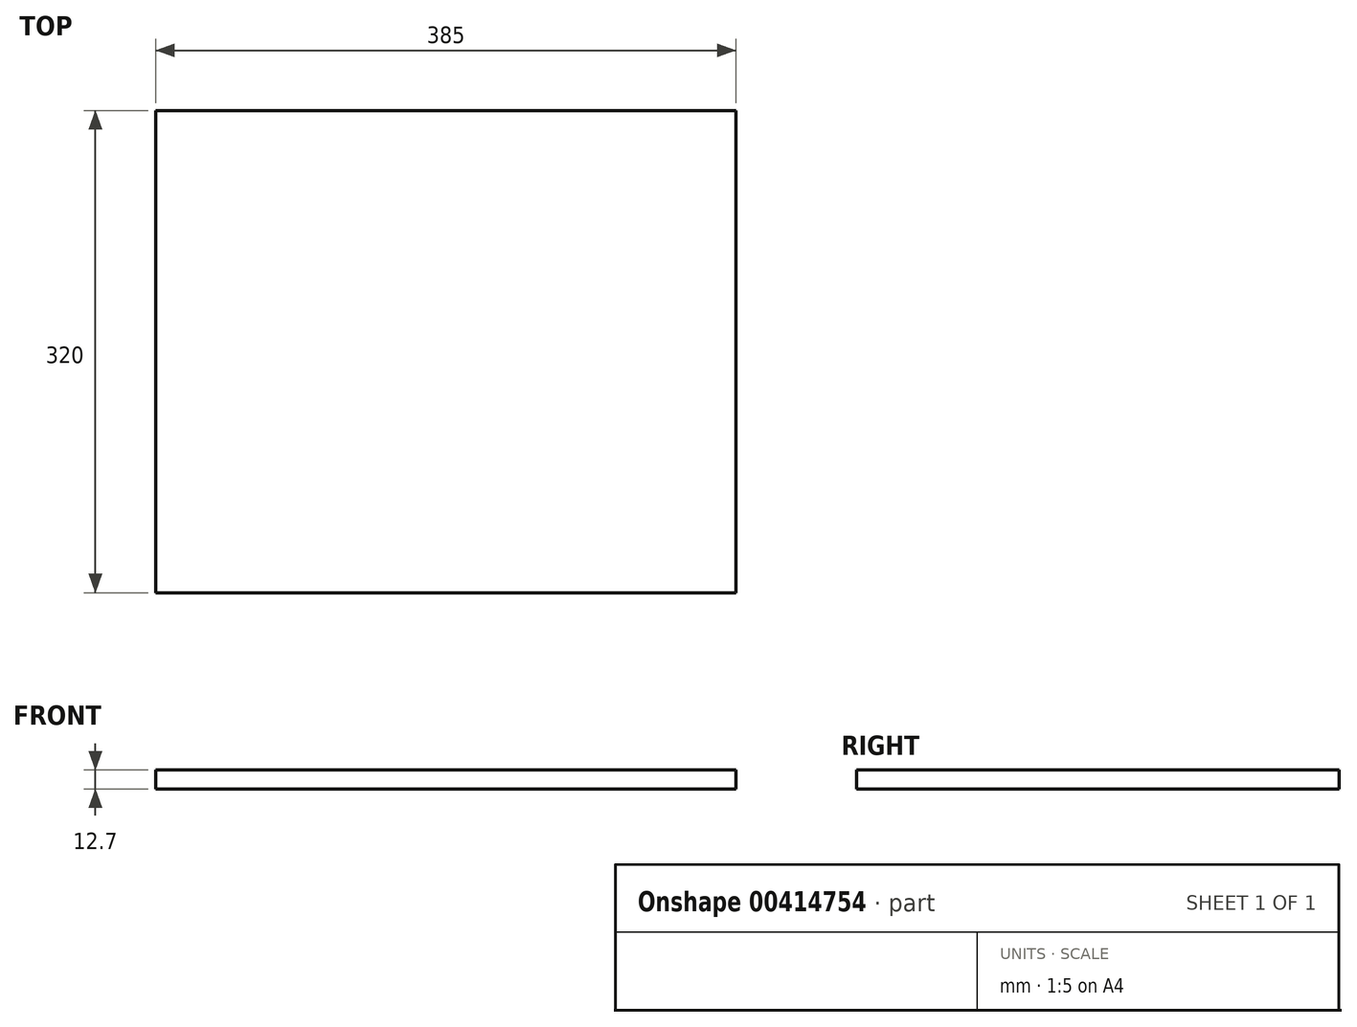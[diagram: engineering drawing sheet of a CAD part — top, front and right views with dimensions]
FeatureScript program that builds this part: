
annotation { "Feature Type Name" : "Feature", "Feature Type Description" : "" }
export const myFeature = defineFeature(function(context is Context, id is Id, definition is map)
    precondition{}
    {
        {
            var Q0;
            Q0=qCreatedBy(makeId("Top.planeOp"),FACE);
            var sketch = newSketch(context, id + "F0", { "sketchPlane" : qUnion([Q0])});
            skLineSegment(sketch, "E0.bottom", {"start": v(-70.96, 65.05) * mm, "end": v(314.04, 65.05) * mm});
            skLineSegment(sketch, "E0.top", {"start": v(-70.96, -254.95) * mm, "end": v(314.04, -254.95) * mm});
            skLineSegment(sketch, "E0.left", {"start": v(-70.96, 65.05) * mm, "end": v(-70.96, -254.95) * mm});
            skLineSegment(sketch, "E0.right", {"start": v(314.04, 65.05) * mm, "end": v(314.04, -254.95) * mm});
            skSolve(sketch);
        }
        {
            var Q0;
            Q0=qSketchRegion(id+"F0",true);
            extrude(context, id + "F1", {"entities" : qUnion([Q0]), "depth" : 12.7 * mm});
        }
    });
